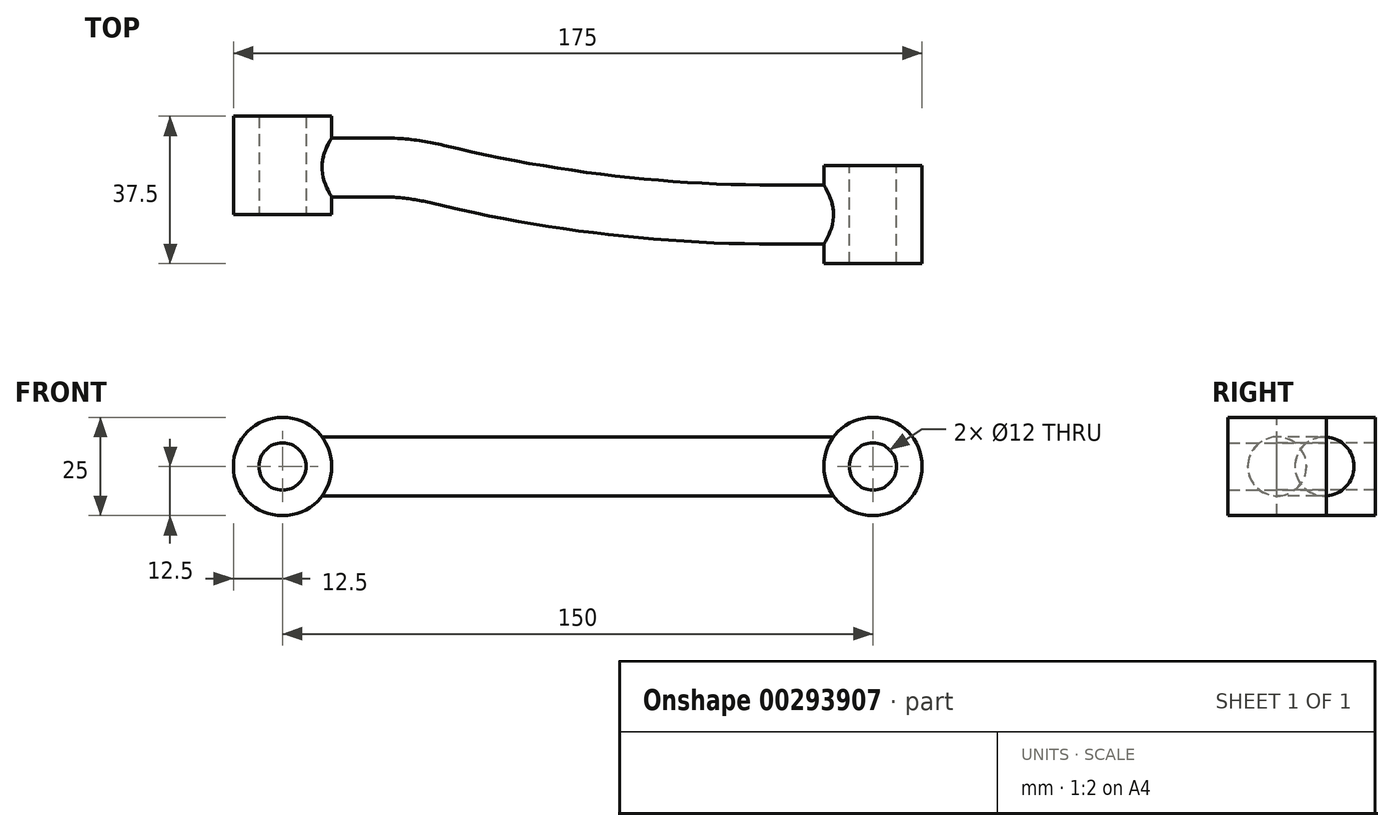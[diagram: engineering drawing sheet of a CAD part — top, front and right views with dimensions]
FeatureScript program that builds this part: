
annotation { "Feature Type Name" : "Feature", "Feature Type Description" : "" }
export const myFeature = defineFeature(function(context is Context, id is Id, definition is map)
    precondition{}
    {
        {
            var Q0;
            Q0=qCreatedBy(makeId("Front.planeOp"),FACE);
            var sketch = newSketch(context, id + "F0", { "sketchPlane" : qUnion([Q0])});
            skCircle(sketch, "E0", {"center": v(0, 0) * mm, "radius": 12.5 * mm});
            skCircle(sketch, "E1", {"center": v(150, 0) * mm, "radius": 12.5 * mm});
            skCircle(sketch, "E2", {"center": v(0, 0) * mm, "radius": 6 * mm});
            skCircle(sketch, "E3", {"center": v(150, 0) * mm, "radius": 6 * mm});
            skSolve(sketch);
        }
        {
            var Q0;
            Q0=makeQuery(id+"F0.imprint","IMPRINT",FACE,{"disambiguationData":[TD([[makeQuery(id+"F0.imprint","IMPRINT",EDGE,{"derivedFrom":sQuery(id+"F0.wireOp",EDGE,"E0")}),1.0]])]});
            extrude(context, id + "F1", {"entities" : qUnion([Q0]), "oppositeDirection" : true, "depth" : 25 * mm});
        }
        {
            var Q0;
            Q0=makeQuery(id+"F0.imprint","IMPRINT",FACE,{"disambiguationData":[TD([[makeQuery(id+"F0.imprint","IMPRINT",EDGE,{"derivedFrom":sQuery(id+"F0.wireOp",EDGE,"E1")}),1.0]])]});
            extrude(context, id + "F2", {"entities" : qUnion([Q0]), "endBound" : BoundingType.SYMMETRIC, "depth" : 25 * mm});
        }
        {
            var Q0;
            Q0=qCreatedBy(makeId("Top.planeOp"),FACE);
            var sketch = newSketch(context, id + "F3", { "sketchPlane" : qUnion([Q0])});
            skLineSegment(sketch, "E4", {"start": v(0, 12) * mm, "end": v(25, 12) * mm});
            skArc(sketch, "E5", {"start": v(25, 12) * mm, "mid": v(32.15, 11.57) * mm, "end": v(39.2, 10.3) * mm});
            skArc(sketch, "E6", {"start": v(39.2, 10.3) * mm, "mid": v(81.79, 2.58) * mm, "end": v(125, 0) * mm});
            skLineSegment(sketch, "E7", {"start": v(125, 0) * mm, "end": v(150, 0) * mm});
            skSolve(sketch);
        }
        {
            var Q0;
            Q0=qCreatedBy(makeId("Right.planeOp"),FACE);
            var sketch = newSketch(context, id + "F4", { "sketchPlane" : qUnion([Q0])});
            skCircle(sketch, "E8", {"center": v(12, 0) * mm, "radius": 7.5 * mm});
            skSolve(sketch);
        }
        {
            var Q0;
            Q0 = qSketchRegion(id + "F4", true);
            var Q1;
            Q1 = qConstructionFilter(qBodyType(qCreatedBy(id + "F3" ,EDGE), BodyType.WIRE), ConstructionObject.NO);
            sweep(context, id + "F5", {"operationType" : NewBodyOperationType.ADD, "profiles" : qUnion([Q0]), "path" : qUnion([Q1])});
        }
        {
            var Q0;
            Q0=makeQuery(id+"F5.opSweep","CAP_FACE",FACE,{"disambiguationData":[OSD([sQuery(id+"F3.wireOp",VERTEX,"E4.start"),sQuery(id+"F4.wireOp",EDGE,"E8")])],"isStart":true});
            var Q1;
            Q1=makeQuery(id+"F1.opExtrude","SWEPT_FACE",FACE,{"disambiguationData":[OSD([sQuery(id+"F0.wireOp",EDGE,"E2")])]});
            extrude(context, id + "F6", {"entities" : qUnion([Q0]), "operationType" : NewBodyOperationType.REMOVE, "endBound" : BoundingType.UP_TO_SURFACE, "oppositeDirection" : true, "endBoundEntityFace" : qUnion([Q1]), "depth" : 25 * mm});
        }
        {
            var Q0;
            Q0=makeQuery(id+"F5.opSweep","CAP_FACE",FACE,{"disambiguationData":[OSD([sQuery(id+"F3.wireOp",VERTEX,"E7.end"),sQuery(id+"F4.wireOp",EDGE,"E8")])],"isStart":false});
            var Q1;
            Q1=makeQuery(id+"F2.opExtrude","SWEPT_FACE",FACE,{"disambiguationData":[OSD([sQuery(id+"F0.wireOp",EDGE,"E3")])]});
            extrude(context, id + "F7", {"entities" : qUnion([Q0]), "operationType" : NewBodyOperationType.REMOVE, "endBound" : BoundingType.UP_TO_SURFACE, "oppositeDirection" : true, "endBoundEntityFace" : qUnion([Q1]), "depth" : 25 * mm});
        }
    });
